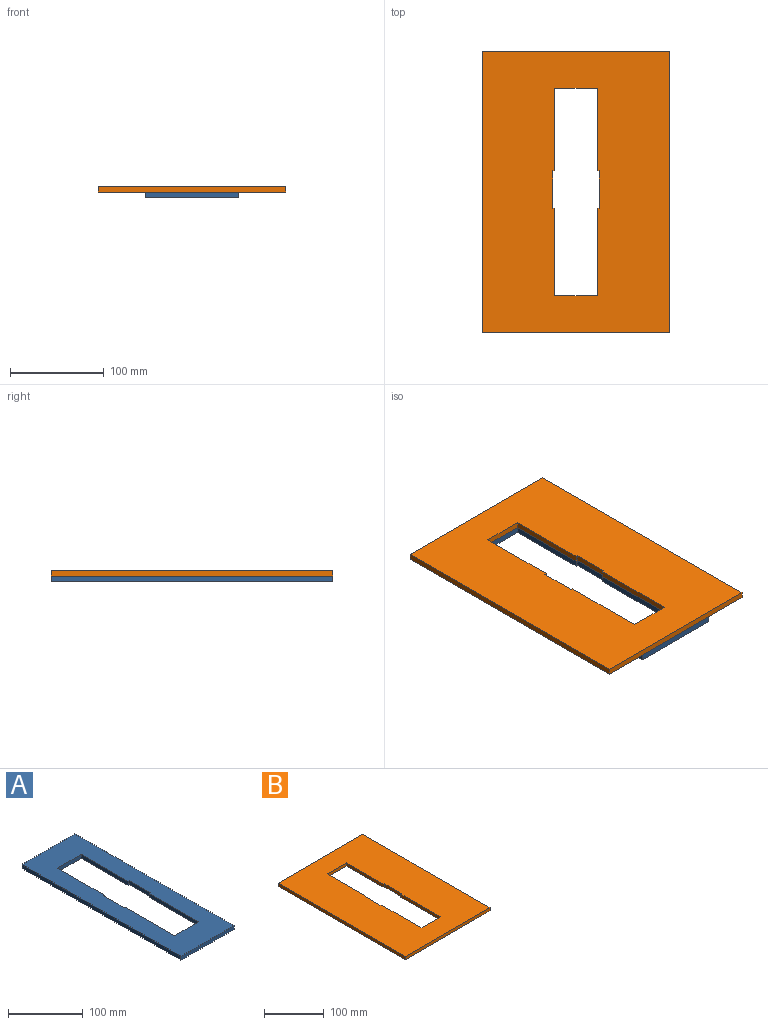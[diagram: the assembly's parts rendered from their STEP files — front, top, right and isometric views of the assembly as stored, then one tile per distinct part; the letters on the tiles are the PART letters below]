
ASSEMBLY  parts=2 mates=1
PART A: 18 faces, bbox 100x300x6.4 mm
  f0: plane 300x100mm, normal (0,0,1), area 19895mm2, adj f2,f3,f4,f5,f6,f7,f8,f9
  f1: plane 300x100mm, normal (0,0,-1), area 19895mm2, adj f2,f3,f4,f5,f6,f7,f8,f9
  f2: plane 100x6.35mm, normal (0,1,0), area 635mm2, adj f0,f1,f3,f5
  f3: plane 300x6.35mm, normal (-1,0,0), area 1905mm2, adj f0,f1,f2,f4
  f4: plane 100x6.35mm, normal (0,-1,0), area 635mm2, adj f0,f1,f3,f5
  f5: plane 300x6.35mm, normal (1,0,0), area 1905mm2, adj f0,f1,f2,f4
  f6: plane 6.35x2mm, normal (0,-1,0), area 12.7mm2, adj f0,f1,f7,f17
  f7: plane 88.02x6.35mm, normal (-1,0,0), area 558.9mm2, adj f0,f1,f6,f8
  f8: plane 45x6.35mm, normal (0,-1,0), area 285.7mm2, adj f0,f1,f7,f9
  f9: plane 88.02x6.35mm, normal (1,0,0), area 558.9mm2, adj f0,f1,f8,f10
  f10: plane 6.35x2mm, normal (0,-1,0), area 12.7mm2, adj f0,f1,f9,f11
  f11: plane 40x6.35mm, normal (1,0,0), area 254mm2, adj f0,f1,f10,f12
  f12: plane 6.35x2mm, normal (0,1,0), area 12.7mm2, adj f0,f1,f11,f13
  f13: plane 92.98x6.35mm, normal (1,0,0), area 590.4mm2, adj f0,f1,f12,f14
  f14: plane 45x6.35mm, normal (0,1,0), area 285.7mm2, adj f0,f1,f13,f15
  f15: plane 92.98x6.35mm, normal (-1,0,0), area 590.4mm2, adj f0,f1,f14,f16
  f16: plane 6.35x2mm, normal (0,1,0), area 12.7mm2, adj f0,f1,f15,f17
  f17: plane 40x6.35mm, normal (-1,0,0), area 254mm2, adj f0,f1,f6,f16
PART B: 18 faces, bbox 200x300x6.4 mm
  f0: plane 300x200mm, normal (0,0,1), area 49895mm2, adj f2,f3,f4,f5,f6,f7,f8,f9
  f1: plane 300x200mm, normal (0,0,-1), area 49895mm2, adj f2,f3,f4,f5,f6,f7,f8,f9
  f2: plane 200x6.35mm, normal (0,1,0), area 1270mm2, adj f0,f1,f3,f5
  f3: plane 300x6.35mm, normal (-1,0,0), area 1905mm2, adj f0,f1,f2,f4
  f4: plane 200x6.35mm, normal (0,-1,0), area 1270mm2, adj f0,f1,f3,f5
  f5: plane 300x6.35mm, normal (1,0,0), area 1905mm2, adj f0,f1,f2,f4
  f6: plane 6.35x2mm, normal (0,-1,0), area 12.7mm2, adj f0,f1,f7,f17
  f7: plane 88.02x6.35mm, normal (-1,0,0), area 558.9mm2, adj f0,f1,f6,f8
  f8: plane 45x6.35mm, normal (0,-1,0), area 285.7mm2, adj f0,f1,f7,f9
  f9: plane 88.02x6.35mm, normal (1,0,0), area 558.9mm2, adj f0,f1,f8,f10
  f10: plane 6.35x2mm, normal (0,-1,0), area 12.7mm2, adj f0,f1,f9,f11
  f11: plane 40x6.35mm, normal (1,0,0), area 254mm2, adj f0,f1,f10,f12
  f12: plane 6.35x2mm, normal (0,1,0), area 12.7mm2, adj f0,f1,f11,f13
  f13: plane 92.98x6.35mm, normal (1,0,0), area 590.4mm2, adj f0,f1,f12,f14
  f14: plane 45x6.35mm, normal (0,1,0), area 285.7mm2, adj f0,f1,f13,f15
  f15: plane 92.98x6.35mm, normal (-1,0,0), area 590.4mm2, adj f0,f1,f14,f16
  f16: plane 6.35x2mm, normal (0,1,0), area 12.7mm2, adj f0,f1,f15,f17
  f17: plane 40x6.35mm, normal (-1,0,0), area 254mm2, adj f0,f1,f6,f16
PLACE A t=(-16.96,-6.78,58.99)mm
PLACE B t=(-16.96,-6.78,65.34)mm
MATE fastened B.f1 <-> A.f0  axis (0,0,-1) through (-41.46,-4.3,65.34)mm
